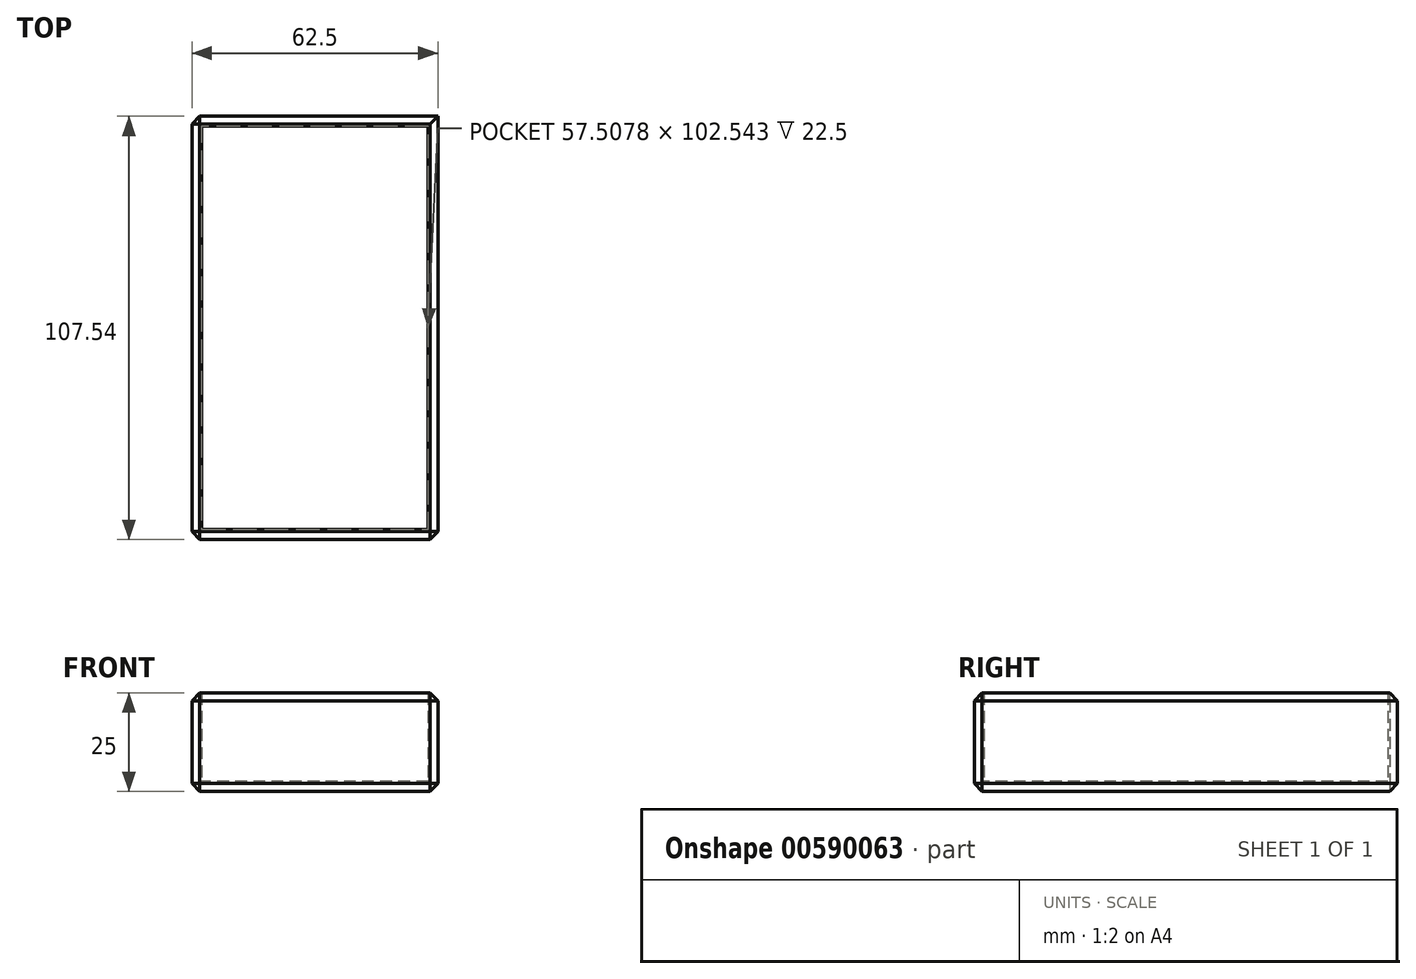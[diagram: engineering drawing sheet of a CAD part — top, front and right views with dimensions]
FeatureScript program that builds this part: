
annotation { "Feature Type Name" : "Feature", "Feature Type Description" : "" }
export const myFeature = defineFeature(function(context is Context, id is Id, definition is map)
    precondition{}
    {
        {
            var Q0;
            Q0=qCreatedBy(makeId("Top.planeOp"),FACE);
            var sketch = newSketch(context, id + "F0", { "sketchPlane" : qUnion([Q0])});
            skLineSegment(sketch, "E0.bottom", {"start": v(31.25, 53.77) * mm, "end": v(-31.25, 53.77) * mm});
            skLineSegment(sketch, "E0.top", {"start": v(31.25, -53.77) * mm, "end": v(-31.25, -53.77) * mm});
            skLineSegment(sketch, "E0.left", {"start": v(31.25, 53.77) * mm, "end": v(31.25, -53.77) * mm});
            skLineSegment(sketch, "E0.right", {"start": v(-31.25, 53.77) * mm, "end": v(-31.25, -53.77) * mm});
            skPoint(sketch, "E0.middle", {"position": v(0, 0) * mm});
            skSolve(sketch);
        }
        {
            var Q0;
            Q0 = qSketchRegion(id + "F0", true);
            extrude(context, id + "F1", {"entities" : qUnion([Q0]), "endBound" : BoundingType.SYMMETRIC, "depth" : 25 * mm, "offsetDistance" : 25 * mm});
        }
        {
            var Q0;
            Q0=makeQuery(id+"F1.opExtrude","CAP_FACE",FACE,{"disambiguationData":[OSD([sQuery(id+"F0.wireOp",EDGE,"E0.bottom"),sQuery(id+"F0.wireOp",EDGE,"E0.top"),sQuery(id+"F0.wireOp",EDGE,"E0.left"),sQuery(id+"F0.wireOp",EDGE,"E0.right")])],"isStart":false});
            shell(context, id + "F2", {"entities" : qUnion([Q0]), "thickness" : 2.5 * mm});
        }
        {
            var Q0;
            Q0=makeQuery(id+"F1.opExtrude","SWEPT_EDGE",EDGE,{"disambiguationData":[OSD([sQuery(id+"F0.wireOp",EDGE,"E0.bottom"),sQuery(id+"F0.wireOp",EDGE,"E0.right")])]});
            var Q1;
            Q1=makeQuery(id+"F1.opExtrude","CAP_EDGE",EDGE,{"disambiguationData":[OSD([sQuery(id+"F0.wireOp",EDGE,"E0.right")])],"isStart":true});
            var Q2;
            Q2=makeQuery(id+"F1.opExtrude","CAP_EDGE",EDGE,{"disambiguationData":[OSD([sQuery(id+"F0.wireOp",EDGE,"E0.right")])],"isStart":false});
            var Q3;
            Q3=makeQuery(id+"F1.opExtrude","CAP_EDGE",EDGE,{"disambiguationData":[OSD([sQuery(id+"F0.wireOp",EDGE,"E0.bottom")])],"isStart":true});
            var Q4;
            Q4=makeQuery(id+"F1.opExtrude","CAP_EDGE",EDGE,{"disambiguationData":[OSD([sQuery(id+"F0.wireOp",EDGE,"E0.bottom")])],"isStart":false});
            var Q5;
            Q5=makeQuery(id+"F1.opExtrude","CAP_EDGE",EDGE,{"disambiguationData":[OSD([sQuery(id+"F0.wireOp",EDGE,"E0.left")])],"isStart":false});
            var Q6;
            Q6=makeQuery(id+"F1.opExtrude","CAP_EDGE",EDGE,{"disambiguationData":[OSD([sQuery(id+"F0.wireOp",EDGE,"E0.left")])],"isStart":true});
            var Q7;
            Q7=makeQuery(id+"F1.opExtrude","SWEPT_EDGE",EDGE,{"disambiguationData":[OSD([sQuery(id+"F0.wireOp",EDGE,"E0.top"),sQuery(id+"F0.wireOp",EDGE,"E0.left")])]});
            var Q8;
            Q8=makeQuery(id+"F1.opExtrude","CAP_EDGE",EDGE,{"disambiguationData":[OSD([sQuery(id+"F0.wireOp",EDGE,"E0.top")])],"isStart":true});
            var Q9;
            Q9=makeQuery(id+"F1.opExtrude","CAP_EDGE",EDGE,{"disambiguationData":[OSD([sQuery(id+"F0.wireOp",EDGE,"E0.top")])],"isStart":false});
            var Q10;
            Q10=makeQuery(id+"F1.opExtrude","SWEPT_EDGE",EDGE,{"disambiguationData":[OSD([sQuery(id+"F0.wireOp",EDGE,"E0.top"),sQuery(id+"F0.wireOp",EDGE,"E0.right")])]});
            chamfer(context, id + "F3", {"entities" : qUnion([Q0, Q1, Q2, Q3, Q4, Q5, Q6, Q7, Q8, Q9, Q10]), "width" : 2 * mm, "tangentPropagation" : true});
        }
    });
